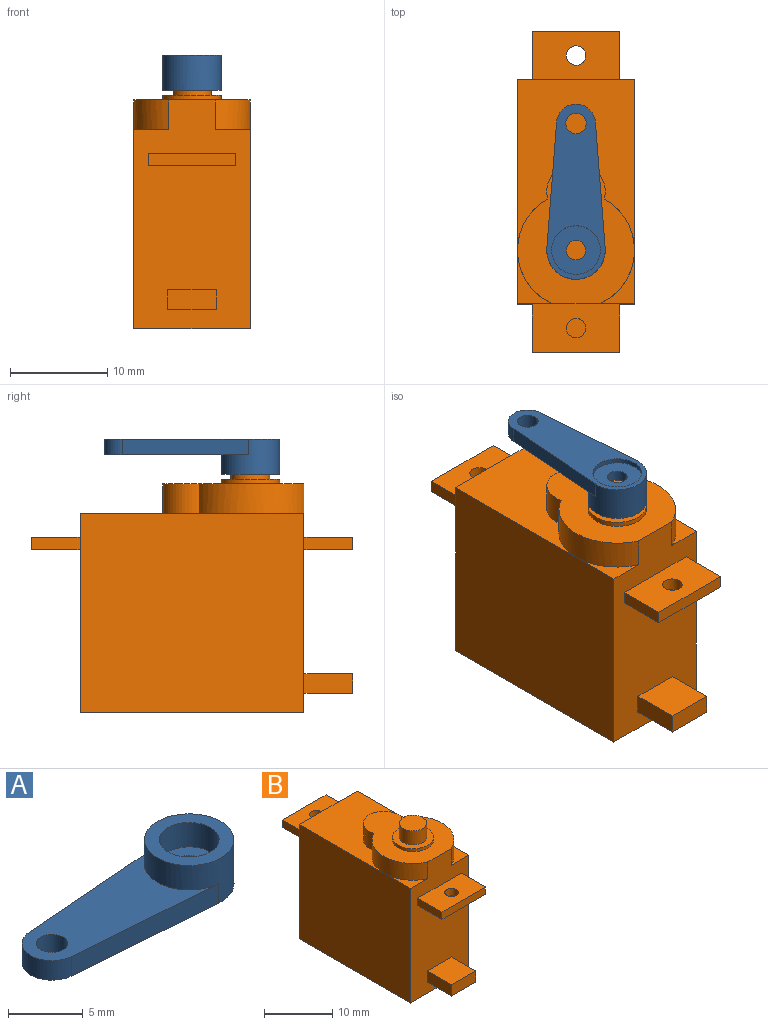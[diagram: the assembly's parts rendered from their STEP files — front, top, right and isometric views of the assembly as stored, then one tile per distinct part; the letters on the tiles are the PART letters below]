
ASSEMBLY  parts=2 mates=1
PART A: 13 faces, bbox 18x6x3.6 mm
  f0: plane 4x4mm, normal (0,0,1), area 9.4mm2, adj f9,f10
  f1: plane 12.92x1.6mm, normal (-0.08,-1,0), area 20.7mm2, adj f2,f4,f6,f8
  f2: cylinder r=3mm len=6mm, axis (0,0,-1), area 53.5mm2, adj f1,f3,f6,f8,f11
  f3: plane 12.92x1.6mm, normal (-0.08,1,0), area 20.7mm2, adj f2,f4,f6,f8
  f4: cylinder r=2mm len=3.99mm, axis (0,0,-1), area 9.6mm2, adj f1,f3,f6,f8
  f5: cylinder r=2.5mm len=5mm, axis (0,0,-1), area 7.9mm2, adj f6,f7
  f6: plane 18x6mm, normal (0,0,-1), area 62.5mm2, adj f1,f2,f3,f4,f5,f12
  f7: plane 5x5mm, normal (0,0,-1), area 16.5mm2, adj f5,f9
  f8: plane 14.77x5.98mm, normal (0,0,1), area 53.9mm2, adj f1,f2,f3,f4,f12
  f9: cylinder r=1mm len=2mm, axis (0,0,-1), area 6.9mm2, adj f0,f7
  f10: cylinder r=2mm len=4mm, axis (0,0,-1), area 25.1mm2, adj f0,f11
  f11: plane 6x6mm, normal (0,0,1), area 15.7mm2, adj f2,f10
  f12: cylinder r=1.05mm len=2.1mm, axis (0,0,1), area 10.6mm2, adj f6,f8
PART B: 33 faces, bbox 12x33x26.5 mm
  f0: plane 23.5x12mm, normal (0,-1,0), area 238.7mm2, adj f1,f2,f3,f4,f7,f8,f10,f11
  f1: plane 5.5x3.6mm, normal (0,0,1), area 5.5mm2, adj f0,f3,f10
  f2: plane 5.5x3.6mm, normal (0,0,1), area 5.5mm2, adj f0,f4,f8
  f3: plane 23x20.5mm, normal (-1,0,0), area 471.5mm2, adj f0,f1,f5,f6,f7
  f4: plane 23x20.5mm, normal (1,0,0), area 471.5mm2, adj f0,f2,f5,f6,f7
  f5: plane 20.5x12mm, normal (0,1,0), area 234.3mm2, adj f3,f4,f6,f7,f22,f24,f26,f27
  f6: plane 17.5x12mm, normal (0,0,1), area 137.8mm2, adj f3,f4,f5,f8,f9,f10
  f7: plane 23x12mm, normal (0,0,-1), area 276mm2, adj f0,f3,f4,f5
  f8: cylinder r=6mm len=10.75mm, axis (0,0,-1), area 40.1mm2, adj f0,f2,f6,f9,f11
  f9: cylinder r=3mm len=6mm, axis (0,0,-1), area 32.8mm2, adj f6,f8,f10,f11
  f10: cylinder r=6mm len=10.75mm, axis (0,0,-1), area 40.1mm2, adj f0,f1,f6,f9,f11
  f11: plane 14.5x12mm, normal (0,0,1), area 98.9mm2, adj f0,f8,f9,f10,f12
  f12: cylinder r=3mm len=6mm, axis (0,0,-1), area 9.4mm2, adj f11,f13
  f13: plane 6x6mm, normal (0,0,1), area 15.7mm2, adj f12,f14
  f14: cylinder r=2mm len=4mm, axis (0,0,-1), area 31.4mm2, adj f13,f15
  f15: plane 4x4mm, normal (0,0,1), area 12.6mm2, adj f14
  f16: plane 5x1.3mm, normal (-1,0,0), area 6.5mm2, adj f0,f17,f20,f21
  f17: plane 9x1.3mm, normal (0,-1,0), area 11.7mm2, adj f16,f19,f20,f21
  f18: cylinder r=1mm len=2mm, axis (0,0,-1), area 8.2mm2, adj f20,f21
  f19: plane 5x1.3mm, normal (1,0,0), area 6.5mm2, adj f0,f17,f20,f21
  f20: plane 9x5mm, normal (0,0,1), area 41.9mm2, adj f0,f16,f17,f18,f19
  f21: plane 9x5mm, normal (0,0,-1), area 41.9mm2, adj f0,f16,f17,f18,f19
  f22: plane 5x1.3mm, normal (1,0,0), area 6.5mm2, adj f5,f23,f26,f27
  f23: plane 9x1.3mm, normal (0,1,0), area 11.7mm2, adj f22,f24,f26,f27
  f24: plane 5x1.3mm, normal (-1,0,0), area 6.5mm2, adj f5,f23,f26,f27
  f25: cylinder r=1mm len=2mm, axis (0,0,-1), area 8.2mm2, adj f26,f27
  f26: plane 9x5mm, normal (0,0,1), area 41.9mm2, adj f5,f22,f23,f24,f25
  f27: plane 9x5mm, normal (0,0,-1), area 41.9mm2, adj f5,f22,f23,f24,f25
  f28: plane 5x2mm, normal (0,-1,0), area 10mm2, adj f29,f30,f31,f32
  f29: plane 5x2mm, normal (1,0,0), area 10mm2, adj f0,f28,f30,f32
  f30: plane 5x5mm, normal (0,0,1), area 25mm2, adj f0,f28,f29,f31
  f31: plane 5x2mm, normal (-1,0,0), area 10mm2, adj f0,f28,f30,f32
  f32: plane 5x5mm, normal (0,0,-1), area 25mm2, adj f0,f28,f29,f31
PLACE A rot(axis=(0.71,-0.71,0),180deg) t=(9.11,-18.17,28.1)mm
PLACE B t=(-2.1,0,0)mm
MATE revolute A.f2 <-> B.f8  axis (0,0,-1) through (-58.74,-57.46,26.5)mm
